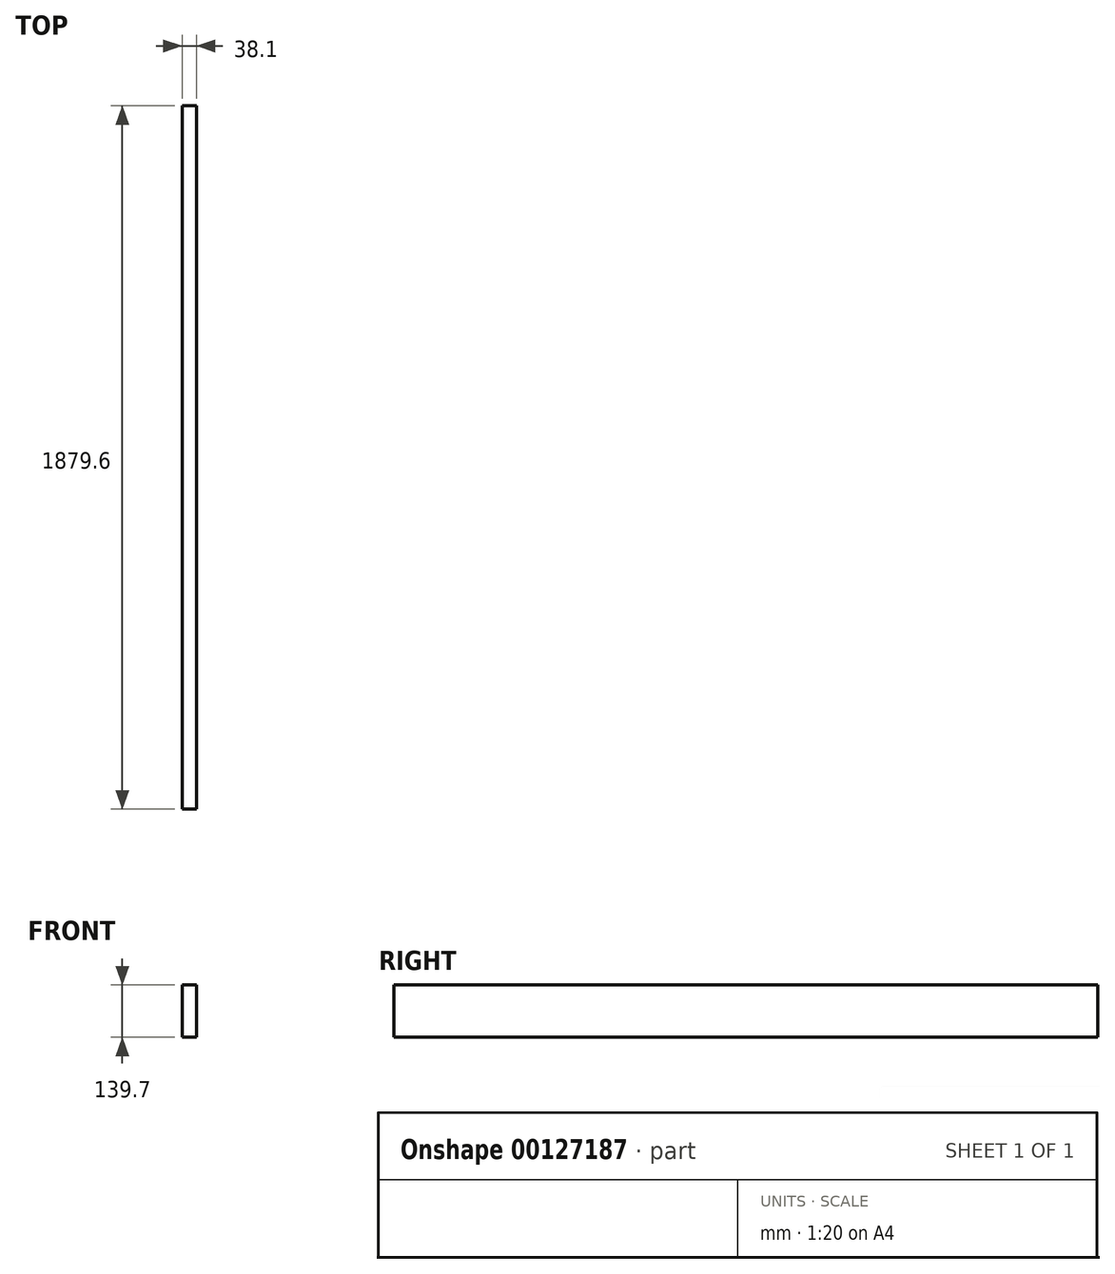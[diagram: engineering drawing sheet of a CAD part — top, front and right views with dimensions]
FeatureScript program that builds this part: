
annotation { "Feature Type Name" : "Feature", "Feature Type Description" : "" }
export const myFeature = defineFeature(function(context is Context, id is Id, definition is map)
    precondition{}
    {
        {
            var Q0;
            Q0=qCreatedBy(makeId("Front.planeOp"),FACE);
            var sketch = newSketch(context, id + "F0", { "sketchPlane" : qUnion([Q0])});
            skLineSegment(sketch, "E0.bottom", {"start": v(-19.05, 69.85) * mm, "end": v(19.05, 69.85) * mm});
            skLineSegment(sketch, "E0.top", {"start": v(-19.05, -69.85) * mm, "end": v(19.05, -69.85) * mm});
            skLineSegment(sketch, "E0.left", {"start": v(-19.05, 69.85) * mm, "end": v(-19.05, -69.85) * mm});
            skLineSegment(sketch, "E0.right", {"start": v(19.05, 69.85) * mm, "end": v(19.05, -69.85) * mm});
            skPoint(sketch, "E0.middle", {"position": v(0, 0) * mm});
            skPoint(sketch, "E1.visualSharp", {"position": v(-19.05, 69.85) * mm});
            skLineSegment(sketch, "E1.filletArc", {"start": v(-19.05, 69.85) * mm, "end": v(-19.05, 69.85) * mm});
            skPoint(sketch, "E2.visualSharp", {"position": v(19.05, 69.85) * mm});
            skLineSegment(sketch, "E2.filletArc", {"start": v(19.05, 69.85) * mm, "end": v(19.05, 69.85) * mm});
            skPoint(sketch, "E3.visualSharp", {"position": v(19.05, -69.85) * mm});
            skLineSegment(sketch, "E3.filletArc", {"start": v(19.05, -69.85) * mm, "end": v(19.05, -69.85) * mm});
            skPoint(sketch, "E4.visualSharp", {"position": v(-19.05, -69.85) * mm});
            skLineSegment(sketch, "E4.filletArc", {"start": v(-19.05, -69.85) * mm, "end": v(-19.05, -69.85) * mm});
            skSolve(sketch);
        }
        {
            var Q0;
            Q0=qSketchRegion(id+"F0",true);
            extrude(context, id + "F1", {"entities" : qUnion([Q0]), "depth" : 1879.6 * mm, "offsetDistance" : 25.4 * mm});
        }
    });
